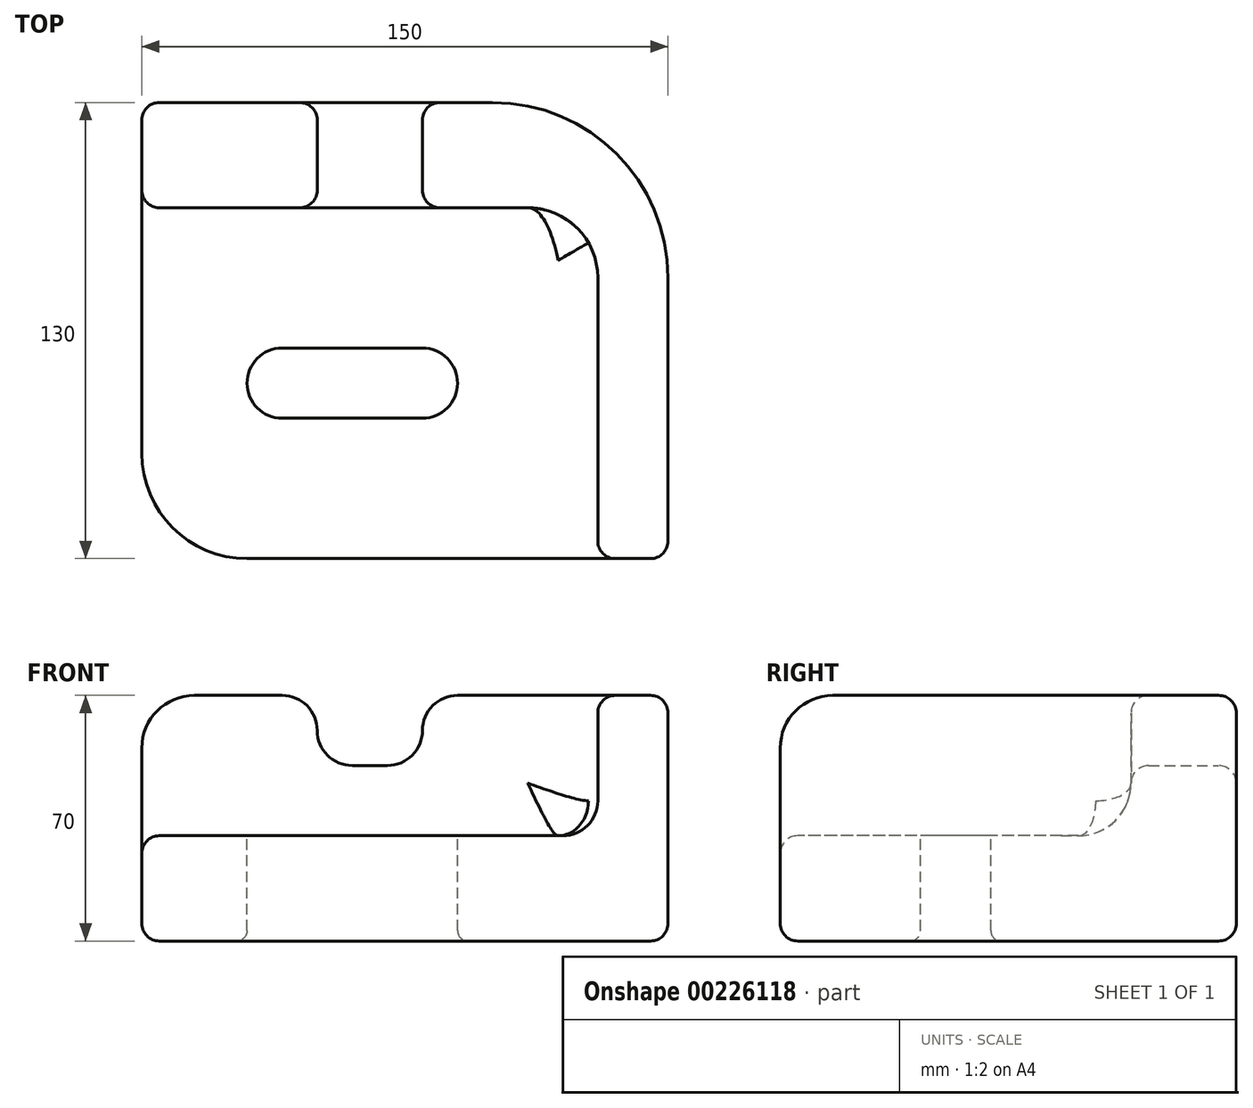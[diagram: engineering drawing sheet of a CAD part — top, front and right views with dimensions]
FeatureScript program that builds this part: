
annotation { "Feature Type Name" : "Feature", "Feature Type Description" : "" }
export const myFeature = defineFeature(function(context is Context, id is Id, definition is map)
    precondition{}
    {
        {
            var Q0;
            Q0=qCreatedBy(makeId("Top.planeOp"),FACE);
            var sketch = newSketch(context, id + "F0", { "sketchPlane" : qUnion([Q0])});
            skLineSegment(sketch, "E0.bottom", {"start": v(0, 130) * mm, "end": v(150, 130) * mm});
            skLineSegment(sketch, "E0.top", {"start": v(0, 0) * mm, "end": v(150, 0) * mm});
            skLineSegment(sketch, "E0.left", {"start": v(0, 130) * mm, "end": v(0, 0) * mm});
            skLineSegment(sketch, "E0.right", {"start": v(150, 130) * mm, "end": v(150, 0) * mm});
            skSolve(sketch);
        }
        {
            var Q0;
            Q0 = qSketchRegion(id + "F0", true);
            extrude(context, id + "F1", {"entities" : qUnion([Q0]), "depth" : 70 * mm});
        }
        {
            var Q0;
            Q0=qCreatedBy(makeId("Top.planeOp"),FACE);
            cPlane(context, id + "F2", {"entities" : qUnion([Q0]), "cplaneType" : CPlaneType.OFFSET, "offset" : 30 * mm, "width" : 150 * mm, "height" : 150 * mm});
        }
        {
            var Q0;
            Q0=qCreatedBy(id+"F2.planeOp",FACE);
            var sketch = newSketch(context, id + "F3", { "sketchPlane" : qUnion([Q0])});
            skLineSegment(sketch, "E1.bottom", {"start": v(-10, 100) * mm, "end": v(130, 100) * mm});
            skLineSegment(sketch, "E1.top", {"start": v(-10, -10) * mm, "end": v(130, -10) * mm});
            skLineSegment(sketch, "E1.left", {"start": v(-10, 100) * mm, "end": v(-10, -10) * mm});
            skLineSegment(sketch, "E1.right", {"start": v(130, 100) * mm, "end": v(130, -10) * mm});
            skSolve(sketch);
        }
        {
            var Q0;
            Q0 = qSketchRegion(id + "F3", true);
            extrude(context, id + "F4", {"entities" : qUnion([Q0]), "operationType" : NewBodyOperationType.REMOVE, "endBound" : BoundingType.THROUGH_ALL, "depth" : 9.95 * mm});
        }
        {
            var Q0;
            Q0=makeQuery(id+"F1.opExtrude","SWEPT_FACE",FACE,{"disambiguationData":[OSD([sQuery(id+"F0.wireOp",EDGE,"E0.bottom")])]});
            var sketch = newSketch(context, id + "F5", { "sketchPlane" : qUnion([Q0])});
            skLineSegment(sketch, "E2.bottom", {"start": v(-80, 80) * mm, "end": v(-50, 80) * mm});
            skLineSegment(sketch, "E2.top", {"start": v(-80, 50) * mm, "end": v(-50, 50) * mm});
            skLineSegment(sketch, "E2.left", {"start": v(-80, 80) * mm, "end": v(-80, 50) * mm});
            skLineSegment(sketch, "E2.right", {"start": v(-50, 80) * mm, "end": v(-50, 50) * mm});
            skSolve(sketch);
        }
        {
            var Q0;
            Q0 = qSketchRegion(id + "F5", true);
            extrude(context, id + "F6", {"entities" : qUnion([Q0]), "operationType" : NewBodyOperationType.REMOVE, "endBound" : BoundingType.THROUGH_ALL, "oppositeDirection" : true, "depth" : 36.85 * mm});
        }
        {
            var Q0;
            Q0=makeQuery(id+"F4.boolean.opBoolean","COPY",FACE,{"derivedFrom":makeQuery(id+"F4.opExtrude","CAP_FACE",FACE,{"disambiguationData":[OSD([sQuery(id+"F3.wireOp",EDGE,"E1.bottom"),sQuery(id+"F3.wireOp",EDGE,"E1.top"),sQuery(id+"F3.wireOp",EDGE,"E1.left"),sQuery(id+"F3.wireOp",EDGE,"E1.right")])],"isStart":true})});
            var sketch = newSketch(context, id + "F7", { "sketchPlane" : qUnion([Q0])});
            skLineSegment(sketch, "E3.bottom", {"start": v(40, 60) * mm, "end": v(80, 60) * mm});
            skLineSegment(sketch, "E3.top", {"start": v(40, 40) * mm, "end": v(80, 40) * mm});
            skLineSegment(sketch, "E3.left", {"start": v(30, 50) * mm, "end": v(30, 40) * mm, "construction": true});
            skLineSegment(sketch, "E3.right", {"start": v(90, 50) * mm, "end": v(90, 40) * mm, "construction": true});
            skArc(sketch, "E4", {"start": v(40, 60) * mm, "mid": v(30, 50) * mm, "end": v(40, 40) * mm});
            skArc(sketch, "E5", {"start": v(80, 40) * mm, "mid": v(90, 50) * mm, "end": v(80, 60) * mm});
            skSolve(sketch);
        }
        {
            var Q0;
            Q0 = qSketchRegion(id + "F7", true);
            extrude(context, id + "F8", {"entities" : qUnion([Q0]), "operationType" : NewBodyOperationType.REMOVE, "endBound" : BoundingType.THROUGH_ALL, "oppositeDirection" : true, "depth" : 96.18 * mm});
        }
        {
            var Q0;
            Q0=makeQuery(id+"F1.opExtrude","SWEPT_EDGE",EDGE,{"disambiguationData":[OSD([sQuery(id+"F0.wireOp",EDGE,"E0.top"),sQuery(id+"F0.wireOp",EDGE,"E0.left")])]});
            fillet(context, id + "F9", {"entities" : qUnion([Q0]), "radius" : 30 * mm, "tangentPropagation" : true, "allowEdgeOverflow" : false});
        }
        {
            var Q0;
            Q0=makeQuery(id+"F1.opExtrude","SWEPT_EDGE",EDGE,{"disambiguationData":[OSD([sQuery(id+"F0.wireOp",EDGE,"E0.bottom"),sQuery(id+"F0.wireOp",EDGE,"E0.right")])]});
            fillet(context, id + "F10", {"entities" : qUnion([Q0]), "radius" : 50 * mm, "tangentPropagation" : true, "allowEdgeOverflow" : false});
        }
        {
            var Q0;
            Q0=makeQuery(id+"F4.boolean.opBoolean","COPY",EDGE,{"derivedFrom":makeQuery(id+"F4.opExtrude","SWEPT_EDGE",EDGE,{"disambiguationData":[OSD([sQuery(id+"F3.wireOp",EDGE,"E1.bottom"),sQuery(id+"F3.wireOp",EDGE,"E1.right")])]})});
            fillet(context, id + "F11", {"entities" : qUnion([Q0]), "radius" : 20 * mm, "tangentPropagation" : true, "allowEdgeOverflow" : false});
        }
        {
            var Q0;
            Q0=makeQuery(id+"F6.boolean.opBoolean","INTERSECT",EDGE,{"derivedFrom":[makeQuery(id+"F1.opExtrude","CAP_FACE",FACE,{"disambiguationData":[OSD([sQuery(id+"F0.wireOp",EDGE,"E0.bottom"),sQuery(id+"F0.wireOp",EDGE,"E0.top"),sQuery(id+"F0.wireOp",EDGE,"E0.left"),sQuery(id+"F0.wireOp",EDGE,"E0.right")])],"isStart":false}),makeQuery(id+"F6.opExtrude","SWEPT_FACE",FACE,{"disambiguationData":[OSD([sQuery(id+"F5.wireOp",EDGE,"E2.right")])]})]});
            var Q1;
            Q1=makeQuery(id+"F6.boolean.opBoolean","COPY",EDGE,{"derivedFrom":makeQuery(id+"F6.opExtrude","SWEPT_EDGE",EDGE,{"disambiguationData":[OSD([sQuery(id+"F5.wireOp",EDGE,"E2.top"),sQuery(id+"F5.wireOp",EDGE,"E2.left")])]})});
            var Q2;
            Q2=makeQuery(id+"F6.boolean.opBoolean","INTERSECT",EDGE,{"derivedFrom":[makeQuery(id+"F1.opExtrude","CAP_FACE",FACE,{"disambiguationData":[OSD([sQuery(id+"F0.wireOp",EDGE,"E0.bottom"),sQuery(id+"F0.wireOp",EDGE,"E0.top"),sQuery(id+"F0.wireOp",EDGE,"E0.left"),sQuery(id+"F0.wireOp",EDGE,"E0.right")])],"isStart":false}),makeQuery(id+"F6.opExtrude","SWEPT_FACE",FACE,{"disambiguationData":[OSD([sQuery(id+"F5.wireOp",EDGE,"E2.left")])]})]});
            var Q3;
            Q3=makeQuery(id+"F6.boolean.opBoolean","COPY",EDGE,{"derivedFrom":makeQuery(id+"F6.opExtrude","SWEPT_EDGE",EDGE,{"disambiguationData":[OSD([sQuery(id+"F5.wireOp",EDGE,"E2.top"),sQuery(id+"F5.wireOp",EDGE,"E2.right")])]})});
            fillet(context, id + "F12", {"entities" : qUnion([Q0, Q1, Q2, Q3]), "radius" : 10 * mm, "tangentPropagation" : true, "allowEdgeOverflow" : false});
        }
        {
            var Q0;
            Q0=makeQuery(id+"F1.opExtrude","CAP_EDGE",EDGE,{"disambiguationData":[OSD([sQuery(id+"F0.wireOp",EDGE,"E0.left")])],"isStart":false});
            var Q1;
            Q1=makeQuery(id+"F1.opExtrude","CAP_EDGE",EDGE,{"disambiguationData":[OSD([sQuery(id+"F0.wireOp",EDGE,"E0.top")])],"isStart":false});
            fillet(context, id + "F13", {"entities" : qUnion([Q0, Q1]), "radius" : 15 * mm, "tangentPropagation" : true, "allowEdgeOverflow" : false});
        }
        {
            var Q0;
            Q0=makeQuery(id+"F1.opExtrude","CAP_EDGE",EDGE,{"disambiguationData":[OSD([sQuery(id+"F0.wireOp",EDGE,"E0.right")])],"isStart":true});
            fillet(context, id + "F14", {"entities" : qUnion([Q0]), "radius" : 5 * mm, "tangentPropagation" : true, "allowEdgeOverflow" : false});
        }
        {
            var Q0;
            Q0=makeQuery(id+"F1.opExtrude","SWEPT_EDGE",EDGE,{"disambiguationData":[OSD([sQuery(id+"F0.wireOp",EDGE,"E0.top"),sQuery(id+"F0.wireOp",EDGE,"E0.right")])]});
            fillet(context, id + "F15", {"entities" : qUnion([Q0]), "radius" : 5 * mm, "tangentPropagation" : true, "allowEdgeOverflow" : false});
        }
        {
            var Q0;
            Q0=makeQuery(id+"F8.boolean.opBoolean","COPY",EDGE,{"derivedFrom":makeQuery(id+"F8.opExtrude","CAP_EDGE",EDGE,{"disambiguationData":[OSD([sQuery(id+"F7.wireOp",EDGE,"E5")])],"isStart":true})});
            var Q1;
            Q1=makeQuery(id+"F8.boolean.opBoolean","INTERSECT",EDGE,{"derivedFrom":[makeQuery(id+"F1.opExtrude","CAP_FACE",FACE,{"disambiguationData":[OSD([sQuery(id+"F0.wireOp",EDGE,"E0.bottom"),sQuery(id+"F0.wireOp",EDGE,"E0.top"),sQuery(id+"F0.wireOp",EDGE,"E0.left"),sQuery(id+"F0.wireOp",EDGE,"E0.right")])],"isStart":true}),makeQuery(id+"F8.opExtrude","SWEPT_FACE",FACE,{"disambiguationData":[OSD([sQuery(id+"F7.wireOp",EDGE,"E5")])]})]});
            fillet(context, id + "F16", {"entities" : qUnion([Q0, Q1]), "radius" : 3 * mm, "tangentPropagation" : true, "allowEdgeOverflow" : false});
        }
        {
            var Q0;
            Q0=makeQuery(id+"F4.boolean.opBoolean","COPY",EDGE,{"derivedFrom":makeQuery(id+"F4.opExtrude","CAP_EDGE",EDGE,{"disambiguationData":[OSD([sQuery(id+"F3.wireOp",EDGE,"E1.right")])],"isStart":true})});
            fillet(context, id + "F17", {"entities" : qUnion([Q0]), "radius" : 10 * mm, "allowEdgeOverflow" : false});
        }
        {
            var Q0;
            Q0=makeQuery(id+"F4.boolean.opBoolean","COPY",EDGE,{"derivedFrom":makeQuery(id+"F4.opExtrude","CAP_EDGE",EDGE,{"disambiguationData":[OSD([sQuery(id+"F3.wireOp",EDGE,"E1.bottom")])],"isStart":true})});
            fillet(context, id + "F18", {"entities" : qUnion([Q0]), "radius" : 15 * mm, "tangentPropagation" : true, "allowEdgeOverflow" : false});
        }
        {
            var Q0;
            Q0=makeQuery(id+"F4.boolean.opBoolean","INTERSECT",EDGE,{"derivedFrom":[makeQuery(id+"F1.opExtrude","CAP_FACE",FACE,{"disambiguationData":[OSD([sQuery(id+"F0.wireOp",EDGE,"E0.bottom"),sQuery(id+"F0.wireOp",EDGE,"E0.top"),sQuery(id+"F0.wireOp",EDGE,"E0.left"),sQuery(id+"F0.wireOp",EDGE,"E0.right")])],"isStart":false}),makeQuery(id+"F4.opExtrude","SWEPT_FACE",FACE,{"disambiguationData":[OSD([sQuery(id+"F3.wireOp",EDGE,"E1.right")])]})]});
            fillet(context, id + "F19", {"entities" : qUnion([Q0]), "radius" : 5 * mm, "tangentPropagation" : true, "allowEdgeOverflow" : false});
        }
    });
